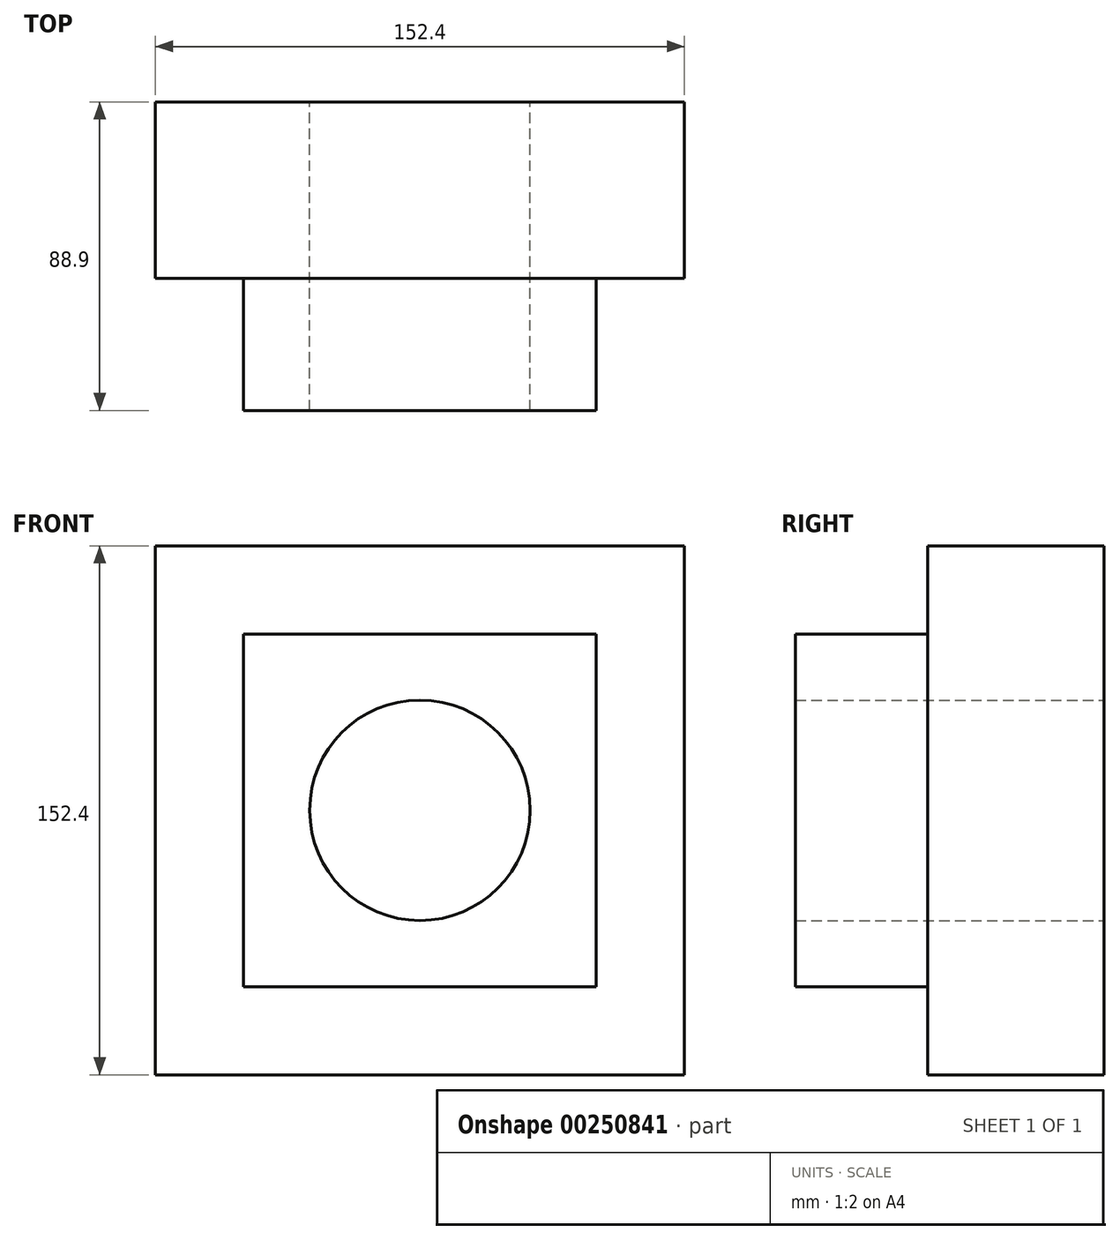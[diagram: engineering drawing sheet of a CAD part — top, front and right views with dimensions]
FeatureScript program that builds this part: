
annotation { "Feature Type Name" : "Feature", "Feature Type Description" : "" }
export const myFeature = defineFeature(function(context is Context, id is Id, definition is map)
    precondition{}
    {
        {
            var Q0;
            Q0=qCreatedBy(makeId("Front.planeOp"),FACE);
            var sketch = newSketch(context, id + "F0", { "sketchPlane" : qUnion([Q0])});
            skCircle(sketch, "E0", {"center": v(0, 0) * mm, "radius": 31.75 * mm});
            skLineSegment(sketch, "E1.bottom", {"start": v(-50.8, 50.8) * mm, "end": v(50.8, 50.8) * mm});
            skLineSegment(sketch, "E1.top", {"start": v(-50.8, -50.8) * mm, "end": v(50.8, -50.8) * mm});
            skLineSegment(sketch, "E1.left", {"start": v(-50.8, 50.8) * mm, "end": v(-50.8, -50.8) * mm});
            skLineSegment(sketch, "E1.right", {"start": v(50.8, 50.8) * mm, "end": v(50.8, -50.8) * mm});
            skLineSegment(sketch, "E2.bottom", {"start": v(-76.2, 76.2) * mm, "end": v(76.2, 76.2) * mm});
            skLineSegment(sketch, "E2.top", {"start": v(-76.2, -76.2) * mm, "end": v(76.2, -76.2) * mm});
            skLineSegment(sketch, "E2.left", {"start": v(-76.2, 76.2) * mm, "end": v(-76.2, -76.2) * mm});
            skLineSegment(sketch, "E2.right", {"start": v(76.2, 76.2) * mm, "end": v(76.2, -76.2) * mm});
            skSolve(sketch);
        }
        {
            var Q0;
            Q0=makeQuery(id+"F0.imprint","IMPRINT",FACE,{"disambiguationData":[TD([[makeQuery(id+"F0.imprint","IMPRINT",EDGE,{"derivedFrom":sQuery(id+"F0.wireOp",EDGE,"E0")}),-1.0]])]});
            extrude(context, id + "F1", {"entities" : qUnion([Q0]), "depth" : 38.1 * mm});
        }
        {
            var Q0;
            Q0=makeQuery(id+"F0.imprint","IMPRINT",FACE,{"disambiguationData":[TD([[makeQuery(id+"F0.imprint","IMPRINT",EDGE,{"derivedFrom":sQuery(id+"F0.wireOp",EDGE,"E1.bottom")}),1.0]])]});
            var Q1;
            Q1=makeQuery(id+"F1.opExtrude","CAP_FACE",FACE,{"disambiguationData":[OSD([sQuery(id+"F0.wireOp",EDGE,"E0"),sQuery(id+"F0.wireOp",EDGE,"E1.bottom"),sQuery(id+"F0.wireOp",EDGE,"E1.top"),sQuery(id+"F0.wireOp",EDGE,"E1.left"),sQuery(id+"F0.wireOp",EDGE,"E1.right")])],"isStart":false});
            extrude(context, id + "F2", {"entities" : qUnion([Q0, Q1]), "operationType" : NewBodyOperationType.ADD, "depth" : 50.8 * mm});
        }
    });
